# Revit family: BWP-SPSW1-FT
name_source: partatom
category: Lighting Fixtures
units: mm (PartAtom-declared; Revit-internal decimal feet)

## family parameters
Cut with Voids When Loaded = Yes
Host = Face
Light Source = Yes
Maintain Annotation Orientation = No
Part Type = Normal
Room Calculation Point = No
Round Connector Dimension = Use Diameter
Shared = No

## types (9) — shared parameters
CRI = 70
Color Filter = 16777215
Default Elevation = 3' - 0"
Dimming Lamp Color Temperature Shift = <None>
Input Voltage = 120V-277V
Lamp = LED
Load Classification = Lighting
Manufacturer = Above All Lighting
Model = BWP-SPSW1-FT
Power Factor = 0.9
Tilt Angle = 90.00°
URL = https://www.abovealllighting.com

## per-type parameters (varying)
| type | Photometric Web File | Wattage Comments |
| BWP-25W-3000K-FT | BWP_SP301_FT_25W.IES | 25W |
| BWP-25W-4000K-FT | BWP_SP401_FT_25W.IES | 25W |
| BWP-25W-5000K-FT | BWP_SP501_FT_25W.IES | 25W |
| BWP-45W-3000K-FT | BWP_SP301_FT_45W.IES | 45W |
| BWP-45W-4000K-FT | BWP_SP401_FT_45W.IES | 45W |
| BWP-45W-5000K-FT | BWP_SP501_FT_45W.IES | 45W |
| BWP-65W-3000K-FT | BWP_SP301_FT_65W.IES | 65W |
| BWP-65W-4000K-FT | BWP_SP401_FT_45W.IES | 65W |
| BWP-65W-5000K-FT | BWP_SP501_FT_65W.IES | 65W |

## geometry (parser evidence)
native form markers: Sweep x2
no freeform markers — native parametric forms only
